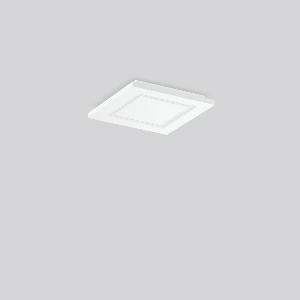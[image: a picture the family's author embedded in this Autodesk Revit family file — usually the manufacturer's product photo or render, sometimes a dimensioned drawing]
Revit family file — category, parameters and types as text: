
# Revit family: hemis_square_312187_002_1_dcdb
name_source: partatom
category: Lighting Fixtures
units: mm (PartAtom-declared; Revit-internal decimal feet)

## family parameters
Cut with Voids When Loaded = No
Host = Face
Light Source = No
Part Type = Normal
Room Calculation Point = No
Round Connector Dimension = Use Diameter
Shared = No

## types (1)
- HEMIS square (1 x LED Modul 840, 1600 lm, 4000)
    Apparent Load = 12 VA
    CIE Flux Codes = 86 99 100 100 100
    Color Rendering = 80
    Color Temperature = 4000
    Default Elevation = 1800 mm
    Description = Series: HEMIS square
Glare-free LED ceiling luminaire with optical lens system. Base: metal, powder-coated, with bayonet fixing. Housing: plastic (polycarbonate). Housing and diffuser are screwed together. Diffuser with optic lenses. Big terminal block; ideal for through-wiring. Sealing strip on the back of the luminaire connects seamlessly with the ceiling. Easy installation with Plug+Play plug connection. Thanks to RUG < 22 ideal for corridors, stairways, shops, schools, meeting rooms, rest areas. 
Colour: white
Length: 250 mm
Width: 250 mm
Height: 33 mm
Lamp: LED
Socket: without socket
Colour temperature: 4000K
Colour rendering index (CRI): 80
System power: 12 W
Rated luminous flux: 1600 lm
Luminous efficiency: 133 lm/W
Control gear: Regulated power supply
Protection class: I
Type of protection: IP 40
    Height = 33 mm
    Lamp = 1 x LED Modul 840
    Lamp Light Flux = 1600 lm
    Lamp count = 1
    Length = 250 mm
    Lifetime = 50000 h
    Luminous efficacy = 133 lm/W
    Manufacturer = RZB
    ModVariant = No
    Model = 312187.002.1
    Mounting Place = Ceiling
    Mounting Type = Surface mounted
    Number of Poles = 1
    OnlyDefault = Yes
    Power Factor = 1
    Product Name = HEMIS square
    Product group = Surface mounted modular luminaires
    ProductGroupID = 306
    Protection Class = Protection class I
    Protection Degree = IP 40
    RLX_Detail_Level = 1
    RLX_Emergency_Light_Flux = 0 lm
    RLX_Emergency_Type = 0
    RLX_Emergency_Type_DB = No
    RlxData = <blob elided: 11481 chars, md5=95d6cbd9>
    Socket = socket
    Standby Power = 0 W
    System Light Flux = 1600 lm
    System Power = 12 W
    Type Comments = Product without accessories
    Type Image = 312187.002.jpg
    URL = http://relux.com
    VarID = ---
    Voltage = 230 V
    Voltage Range = 220-240 V
    Weight = 0.00 kg
    Width = 250 mm

## geometry (parser evidence)
native form markers: Sweep x9
no freeform markers — native parametric forms only
